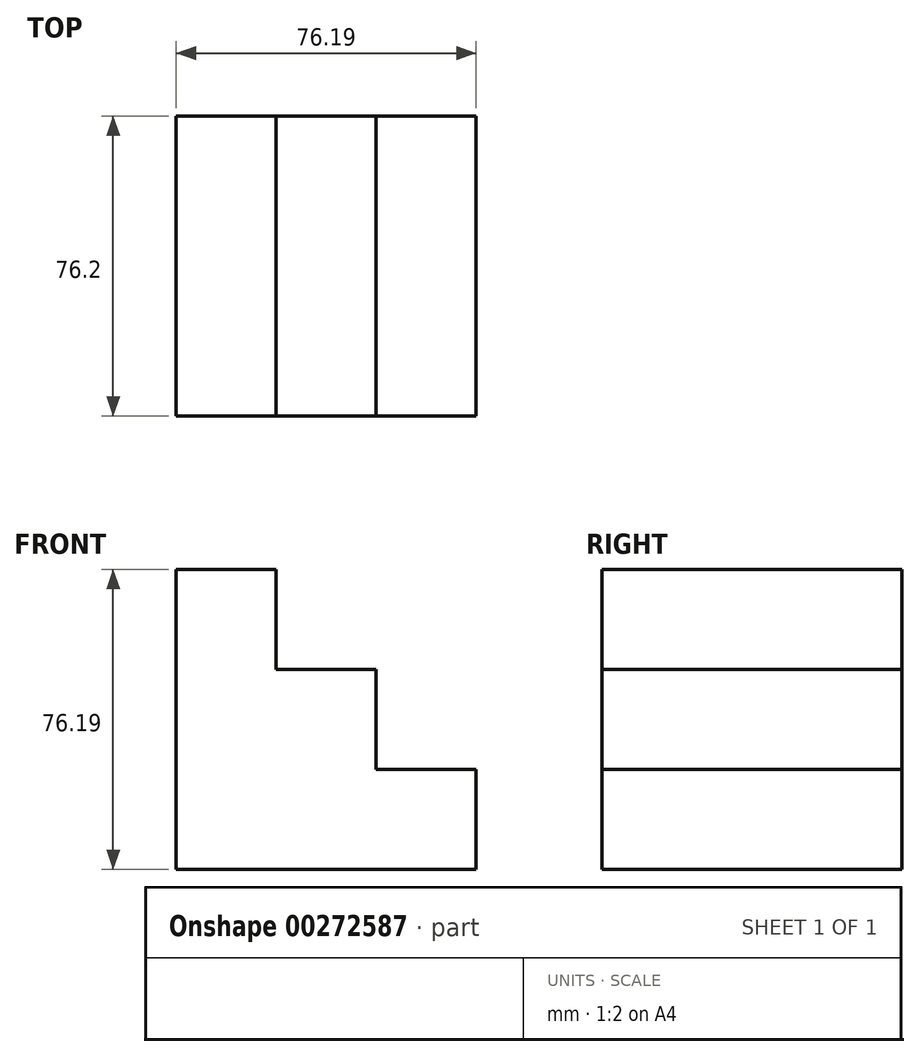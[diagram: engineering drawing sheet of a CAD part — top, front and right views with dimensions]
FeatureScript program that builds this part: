
annotation { "Feature Type Name" : "Feature", "Feature Type Description" : "" }
export const myFeature = defineFeature(function(context is Context, id is Id, definition is map)
    precondition{}
    {
        {
            var Q0;
            Q0=qCreatedBy(makeId("Front.planeOp"),FACE);
            var sketch = newSketch(context, id + "F0", { "sketchPlane" : qUnion([Q0])});
            skLineSegment(sketch, "E0", {"start": v(-54.42, 54.04) * mm, "end": v(-54.42, -22.15) * mm});
            skLineSegment(sketch, "E1", {"start": v(-54.42, -22.15) * mm, "end": v(21.77, -22.15) * mm});
            skLineSegment(sketch, "E2", {"start": v(21.77, -22.15) * mm, "end": v(21.77, 3.25) * mm});
            skLineSegment(sketch, "E3", {"start": v(21.77, 3.25) * mm, "end": v(-3.63, 3.25) * mm});
            skLineSegment(sketch, "E4", {"start": v(-3.63, 3.25) * mm, "end": v(-3.63, 28.64) * mm});
            skLineSegment(sketch, "E5", {"start": v(-3.63, 28.64) * mm, "end": v(-29.03, 28.64) * mm});
            skLineSegment(sketch, "E6", {"start": v(-29.03, 28.64) * mm, "end": v(-29.03, 54.04) * mm});
            skLineSegment(sketch, "E7", {"start": v(-29.03, 54.04) * mm, "end": v(-54.42, 54.04) * mm});
            skSolve(sketch);
        }
        {
            var Q0;
            Q0=makeQuery(id+"F0.imprint","IMPRINT",FACE,{"disambiguationData":[TD([[makeQuery(id+"F0.imprint","IMPRINT",EDGE,{"derivedFrom":sQuery(id+"F0.wireOp",EDGE,"E0")}),1.0]])]});
            extrude(context, id + "F1", {"entities" : qUnion([Q0]), "depth" : 76.2 * mm});
        }
    });
